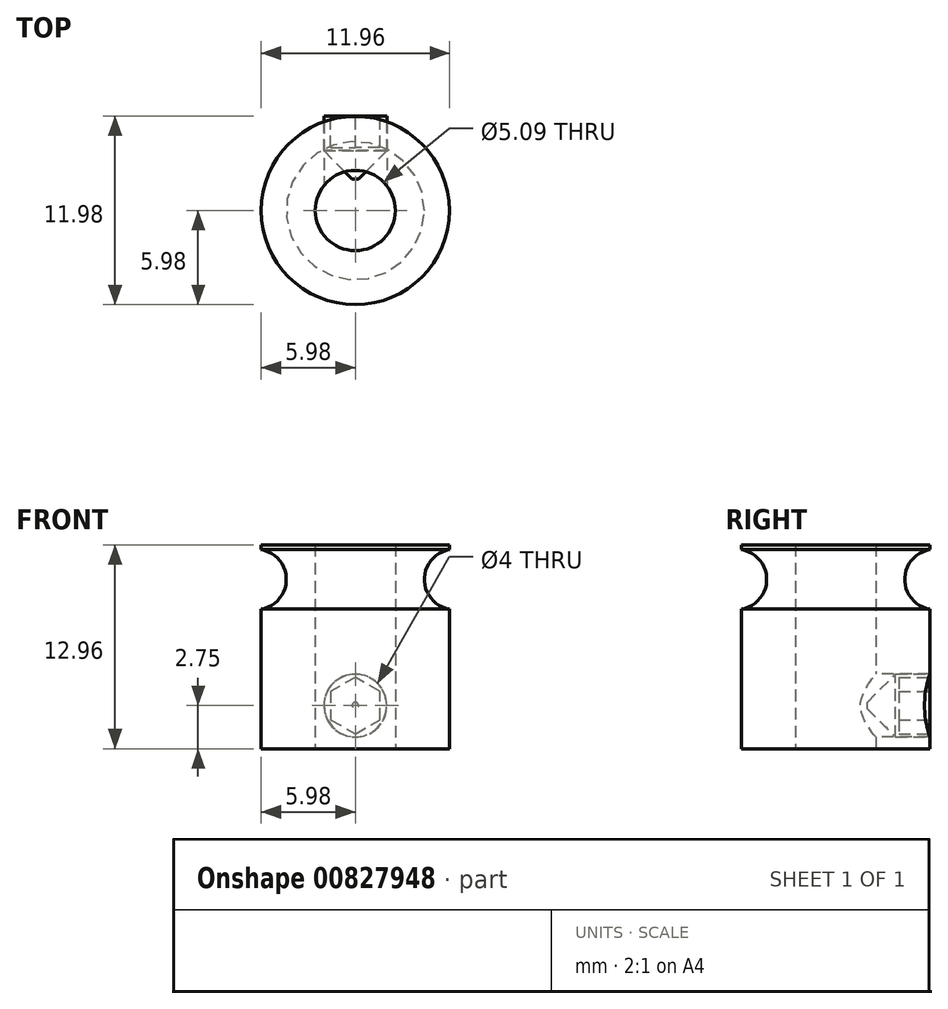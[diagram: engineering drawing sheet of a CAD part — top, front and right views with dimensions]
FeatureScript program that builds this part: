
annotation { "Feature Type Name" : "Feature", "Feature Type Description" : "" }
export const myFeature = defineFeature(function(context is Context, id is Id, definition is map)
    precondition{}
    {
        {
            var Q0;
            Q0=qCreatedBy(makeId("Top.planeOp"),FACE);
            var sketch = newSketch(context, id + "F0", { "sketchPlane" : qUnion([Q0])});
            skCircle(sketch, "E0", {"center": v(0, 0) * mm, "radius": 5.98 * mm});
            skCircle(sketch, "E1", {"center": v(0, 0) * mm, "radius": 2.54 * mm});
            skSolve(sketch);
        }
        {
            var Q0;
            Q0=makeQuery(id+"F0.imprint","IMPRINT",FACE,{"disambiguationData":[TD([[makeQuery(id+"F0.imprint","IMPRINT",EDGE,{"derivedFrom":sQuery(id+"F0.wireOp",EDGE,"E0")}),1.0]])]});
            extrude(context, id + "F1", {"entities" : qUnion([Q0]), "depth" : 12.96 * mm, "offsetDistance" : 25 * mm});
        }
        {
            var Q0;
            Q0=qCreatedBy(makeId("Front.planeOp"),FACE);
            var sketch = newSketch(context, id + "F2", { "sketchPlane" : qUnion([Q0])});
            skCircle(sketch, "E2", {"center": v(0, 2.75) * mm, "radius": 2 * mm});
            skSolve(sketch);
        }
        {
            var Q0;
            Q0 = qSketchRegion(id + "F2", true);
            extrude(context, id + "F3", {"entities" : qUnion([Q0]), "operationType" : NewBodyOperationType.REMOVE, "endBound" : BoundingType.THROUGH_ALL, "oppositeDirection" : true, "depth" : 25 * mm, "offsetDistance" : 25 * mm});
        }
        {
            var Q0;
            Q0=qCreatedBy(makeId("Top.planeOp"),FACE);
            cPlane(context, id + "F4", {"entities" : qUnion([Q0]), "cplaneType" : CPlaneType.OFFSET, "offset" : 10.76 * mm, "width" : 150 * mm, "height" : 150 * mm});
        }
        {
            var Q0;
            Q0=qCreatedBy(id+"F4.planeOp",FACE);
            var sketch = newSketch(context, id + "F5", { "sketchPlane" : qUnion([Q0])});
            skCircle(sketch, "E3", {"center": v(0, 0) * mm, "radius": 6.3 * mm});
            skSolve(sketch);
        }
        {
            var Q0;
            Q0=qCreatedBy(makeId("Front.planeOp"),FACE);
            var sketch = newSketch(context, id + "F6", { "sketchPlane" : qUnion([Q0])});
            skCircle(sketch, "E4", {"center": v(6.3, 10.76) * mm, "radius": 1.92 * mm});
            skSolve(sketch);
        }
        {
            var Q0;
            Q0=makeQuery(id+"F6.imprint","IMPRINT",FACE,{"disambiguationData":[TD([[makeQuery(id+"F6.imprint","IMPRINT",EDGE,{"derivedFrom":sQuery(id+"F6.wireOp",EDGE,"E4")}),1.0]])]});
            var Q1;
            Q1=sQuery(id+"F5.wireOp",EDGE,"E3");
            sweep(context, id + "F7", {"profiles" : qUnion([Q0]), "path" : qUnion([Q1])});
        }
        {
            var Q0;
            Q0=makeQuery(id+"F7.opSweep","SWEPT_BODY",BODY,{"disambiguationData":[OSD([sQuery(id+"F5.wireOp",EDGE,"E3"),sQuery(id+"F6.wireOp",EDGE,"E4")])]});
            var Q1;
            Q1=makeQuery(id+"F1.opExtrude","SWEPT_BODY",BODY,{"disambiguationData":[OSD([sQuery(id+"F0.wireOp",EDGE,"E0"),sQuery(id+"F0.wireOp",EDGE,"E1")])]});
            booleanBodies(context, id + "F8", {"operationType" : BooleanOperationType.SUBTRACTION, "tools" : qUnion([Q0]), "targets" : qUnion([Q1])});
        }
        {
            var Q0;
            Q0=qCreatedBy(makeId("Front.planeOp"),FACE);
            cPlane(context, id + "F9", {"entities" : qUnion([Q0]), "cplaneType" : CPlaneType.OFFSET, "offset" : 6 * mm, "oppositeDirection" : true, "width" : 150 * mm, "height" : 150 * mm});
        }
        {
            var Q0;
            Q0=qCreatedBy(id+"F9.planeOp",FACE);
            var sketch = newSketch(context, id + "F10", { "sketchPlane" : qUnion([Q0])});
            skCircle(sketch, "E5", {"center": v(0, 2.75) * mm, "radius": 2 * mm});
            skCircle(sketch, "E6.0", {"center": v(0, 2.75) * mm, "radius": 2 * mm, "construction": true});
            skSolve(sketch);
        }
        {
            var Q0;
            Q0 = qSketchRegion(id + "F10", true);
            extrude(context, id + "F11", {"entities" : qUnion([Q0]), "depth" : 4 * mm, "offsetDistance" : 25 * mm});
        }
        {
            var Q0;
            Q0=makeQuery(id+"F11.opExtrude","CAP_EDGE",EDGE,{"disambiguationData":[OSD([sQuery(id+"F10.wireOp",EDGE,"E5")])],"isStart":false});
            chamfer(context, id + "F12", {"entities" : qUnion([Q0]), "width" : 1.8 * mm, "tangentPropagation" : true});
        }
        {
            var Q0;
            Q0=makeQuery(id+"F11.opExtrude","CAP_FACE",FACE,{"disambiguationData":[OSD([sQuery(id+"F10.wireOp",EDGE,"E5")])],"isStart":true});
            var sketch = newSketch(context, id + "F13", { "sketchPlane" : qUnion([Q0])});
            skCircle(sketch, "E7.cCircle", {"center": v(0, 2.75) * mm, "radius": 1.8 * mm, "construction": true});
            skLineSegment(sketch, "E7.0", {"start": v(1.56, 1.85) * mm, "end": v(0, 0.95) * mm});
            skLineSegment(sketch, "E7.1", {"start": v(0, 0.95) * mm, "end": v(-1.56, 1.85) * mm});
            skLineSegment(sketch, "E7.2", {"start": v(-1.56, 1.85) * mm, "end": v(-1.56, 3.65) * mm});
            skLineSegment(sketch, "E7.3", {"start": v(-1.56, 3.65) * mm, "end": v(0, 4.55) * mm});
            skLineSegment(sketch, "E7.4", {"start": v(0, 4.55) * mm, "end": v(1.56, 3.65) * mm});
            skLineSegment(sketch, "E7.5", {"start": v(1.56, 3.65) * mm, "end": v(1.56, 1.85) * mm});
            skSolve(sketch);
        }
        {
            var Q0;
            Q0 = qSketchRegion(id + "F13", true);
            extrude(context, id + "F14", {"entities" : qUnion([Q0]), "operationType" : NewBodyOperationType.REMOVE, "oppositeDirection" : true, "depth" : 2 * mm, "offsetDistance" : 25 * mm});
        }
    });
